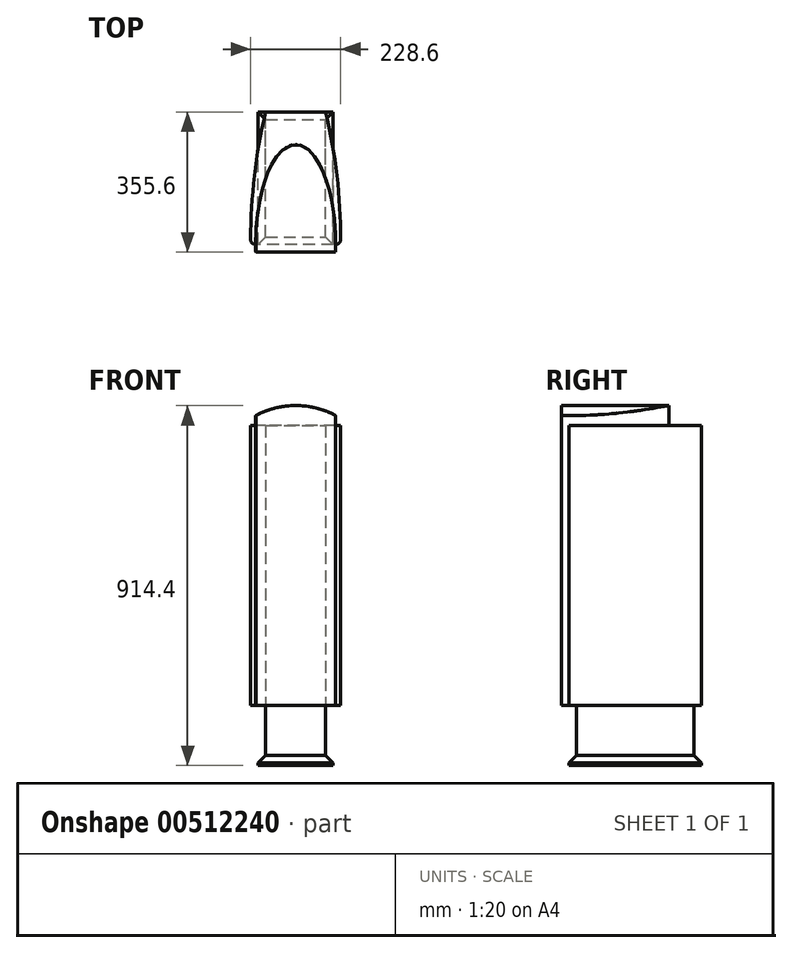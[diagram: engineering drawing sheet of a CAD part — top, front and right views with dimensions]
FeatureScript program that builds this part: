
annotation { "Feature Type Name" : "Feature", "Feature Type Description" : "" }
export const myFeature = defineFeature(function(context is Context, id is Id, definition is map)
    precondition{}
    {
        {
            var Q0;
            Q0=qCreatedBy(makeId("Top.planeOp"),FACE);
            var sketch = newSketch(context, id + "F0", { "sketchPlane" : qUnion([Q0])});
            skLineSegment(sketch, "E0.bottom", {"start": v(-114.3, -177.8) * mm, "end": v(114.3, -177.8) * mm});
            skLineSegment(sketch, "E0.top", {"start": v(-114.3, 177.8) * mm, "end": v(114.3, 177.8) * mm});
            skLineSegment(sketch, "E0.left", {"start": v(-114.3, -177.8) * mm, "end": v(-114.3, 177.8) * mm});
            skLineSegment(sketch, "E0.right", {"start": v(114.3, -177.8) * mm, "end": v(114.3, 177.8) * mm});
            skPoint(sketch, "E0.middle", {"position": v(0, 0) * mm});
            skLineSegment(sketch, "E1.bottom", {"start": v(-114.3, -177.8) * mm, "end": v(-101.6, -177.8) * mm});
            skLineSegment(sketch, "E1.top", {"start": v(-114.3, -146.05) * mm, "end": v(-101.6, -146.05) * mm});
            skLineSegment(sketch, "E1.left", {"start": v(-114.3, -177.8) * mm, "end": v(-114.3, -146.05) * mm});
            skLineSegment(sketch, "E1.right", {"start": v(-101.6, -177.8) * mm, "end": v(-101.6, -146.05) * mm});
            skArc(sketch, "E2", {"start": v(-114.3, -146.05) * mm, "mid": v(-104.74, 17) * mm, "end": v(-76.2, 177.8) * mm});
            skLineSegment(sketch, "E3.bottom", {"start": v(114.3, -177.8) * mm, "end": v(101.6, -177.8) * mm});
            skLineSegment(sketch, "E3.top", {"start": v(114.3, -146.05) * mm, "end": v(101.6, -146.05) * mm});
            skLineSegment(sketch, "E3.left", {"start": v(114.3, -177.8) * mm, "end": v(114.3, -146.05) * mm});
            skLineSegment(sketch, "E3.right", {"start": v(101.6, -177.8) * mm, "end": v(101.6, -146.05) * mm});
            skArc(sketch, "E4", {"start": v(114.3, -146.05) * mm, "mid": v(104.74, 17) * mm, "end": v(76.2, 177.8) * mm});
            skArc(sketch, "E5", {"start": v(-114.3, -146.05) * mm, "mid": v(-110.58, -155.03) * mm, "end": v(-101.6, -158.75) * mm});
            skArc(sketch, "E6", {"start": v(114.3, -146.05) * mm, "mid": v(110.58, -155.03) * mm, "end": v(101.6, -158.75) * mm});
            skLineSegment(sketch, "E7", {"start": v(-101.6, -158.75) * mm, "end": v(101.6, -158.75) * mm});
            skEllipse(sketch, "E8", {"center": v(0, -158.75) * mm, "majorRadius": 101.6 * mm, "minorRadius": 254 * mm, "majorAxis": v(-1, 0)});
            skLineSegment(sketch, "E9.bottom", {"start": v(-76.2, -139.7) * mm, "end": v(76.2, -139.7) * mm});
            skLineSegment(sketch, "E9.top", {"start": v(-76.2, 158.75) * mm, "end": v(76.2, 158.75) * mm});
            skLineSegment(sketch, "E9.left", {"start": v(-76.2, -139.7) * mm, "end": v(-76.2, 158.75) * mm});
            skLineSegment(sketch, "E9.right", {"start": v(76.2, -139.7) * mm, "end": v(76.2, 158.75) * mm});
            skSolve(sketch);
        }
        {
            var Q0;
            {var subQ7=sQuery(id+"F0.wireOp",EDGE,"E1.top");Q0=makeQuery(id+"F0.imprint","IMPRINT",FACE,{"disambiguationData":[TD([[makeQuery(id+"F0.imprint","IMPRINT",EDGE,{"derivedFrom":subQ7}),1.0]])]});}
            var Q1;
            {var subQ0=sQuery(id+"F0.wireOp",EDGE,"E1.top");Q1=makeQuery(id+"F0.imprint","IMPRINT",FACE,{"disambiguationData":[TD([[makeQuery(id+"F0.imprint","IMPRINT",EDGE,{"derivedFrom":subQ0}),-1.0]])]});}
            var Q2;
            {var subQ0=sQuery(id+"F0.wireOp",EDGE,"E3.top");Q2=makeQuery(id+"F0.imprint","IMPRINT",FACE,{"disambiguationData":[TD([[makeQuery(id+"F0.imprint","IMPRINT",EDGE,{"derivedFrom":subQ0}),1.0]])]});}
            var Q3;
            {var subQ5=sQuery(id+"F0.wireOp",EDGE,"E9.top");Q3=makeQuery(id+"F0.imprint","IMPRINT",FACE,{"disambiguationData":[TD([[makeQuery(id+"F0.imprint","IMPRINT",EDGE,{"derivedFrom":subQ5}),-1.0]])]});}
            extrude(context, id + "F1", {"entities" : qUnion([Q0, Q1, Q2, Q3]), "depth" : 711.2 * mm});
        }
        {
            var Q0;
            {var subQ0=sQuery(id+"F0.wireOp",EDGE,"E7");Q0=makeQuery(id+"F0.imprint","IMPRINT",FACE,{"disambiguationData":[TD([[makeQuery(id+"F0.imprint","IMPRINT",EDGE,{"derivedFrom":subQ0}),1.0]])]});}
            var Q1;
            {var subQ4=sQuery(id+"F0.wireOp",EDGE,"E7");Q1=makeQuery(id+"F0.imprint","IMPRINT",FACE,{"disambiguationData":[TD([[makeQuery(id+"F0.imprint","IMPRINT",EDGE,{"derivedFrom":subQ4}),-1.0]])]});}
            var Q2;
            {var subQ5=sQuery(id+"F0.wireOp",EDGE,"E9.bottom");Q2=makeQuery(id+"F0.imprint","IMPRINT",FACE,{"disambiguationData":[TD([[makeQuery(id+"F0.imprint","IMPRINT",EDGE,{"derivedFrom":subQ5}),1.0]])]});}
            extrude(context, id + "F2", {"entities" : qUnion([Q0, Q1, Q2]), "operationType" : NewBodyOperationType.ADD, "depth" : 762 * mm});
        }
        {
            var Q0;
            Q0=makeQuery(id+"F2.opExtrude","SWEPT_FACE",FACE,{"disambiguationData":[OSD([sQuery(id+"F0.wireOp",EDGE,"E0.bottom")])]});
            var sketch = newSketch(context, id + "F3", { "sketchPlane" : qUnion([Q0])});
            skArc(sketch, "E10", {"start": v(101.31, 736.6) * mm, "mid": v(0, 762) * mm, "end": v(-101.31, 736.6) * mm});
            skSolve(sketch);
        }
        {
            var Q0;
            {var subQ0=sQuery(id+"F3.wireOp",EDGE,"E10");var subQ2=sQuery(id+"F0.wireOp",EDGE,"E0.bottom");var subQ5=makeQuery(id+"F2.opExtrude","CAP_EDGE",EDGE,{"disambiguationData":[OSD([subQ2])],"isStart":false});var subQ6=makeQuery(id+"F3.imprint","INTERSECT",VERTEX,{"derivedFrom":[subQ5,subQ0]});Q0=makeQuery(id+"F3.imprint","IMPRINT",FACE,{"disambiguationData":[TD([[makeQuery(id+"F3.imprint","IMPRINT",EDGE,{"disambiguationData":[TD([[subQ6,-1.0]])],"derivedFrom":subQ0}),-1.0]])]});}
            var Q1;
            {var subQ0=sQuery(id+"F3.wireOp",EDGE,"E10");var subQ2=sQuery(id+"F0.wireOp",EDGE,"E0.bottom");var subQ5=makeQuery(id+"F2.opExtrude","CAP_EDGE",EDGE,{"disambiguationData":[OSD([subQ2])],"isStart":false});var subQ6=makeQuery(id+"F3.imprint","INTERSECT",VERTEX,{"derivedFrom":[subQ5,subQ0]});Q1=makeQuery(id+"F3.imprint","IMPRINT",FACE,{"disambiguationData":[TD([[makeQuery(id+"F3.imprint","IMPRINT",EDGE,{"disambiguationData":[TD([[subQ6,1.0]])],"derivedFrom":subQ0}),-1.0]])]});}
            extrude(context, id + "F4", {"entities" : qUnion([Q0, Q1]), "operationType" : NewBodyOperationType.REMOVE, "endBound" : BoundingType.UP_TO_NEXT, "oppositeDirection" : true, "depth" : 25.4 * mm});
        }
        {
            var Q0;
            {var subQ0=sQuery(id+"F0.wireOp",EDGE,"E0.bottom");var subQ1=sQuery(id+"F0.wireOp",EDGE,"E8");var subQ2=makeQuery(id+"F2.opExtrude","SWEPT_EDGE",EDGE,{"disambiguationData":[OSD([subQ0,subQ1]),TDD([makeQuery(id+"F0.imprint","INTERSECT",VERTEX,{"disambiguationData":[OD(0.0)],"derivedFrom":[subQ0,subQ1]})])]});Q0=makeQuery(id+"F4.boolean.opBoolean","COPY",FACE,{"derivedFrom":makeQuery(id+"F4.opExtrude","SWEPT_FACE",FACE,{"disambiguationData":[OSD([subQ0,subQ1]),TDD([makeQuery(id+"F3.imprint","IMPRINT",EDGE,{"disambiguationData":[TD([[makeQuery(id+"F3.imprint","INTERSECT",VERTEX,{"derivedFrom":[subQ2,makeQuery(id+"F2.opExtrude","CAP_EDGE",EDGE,{"disambiguationData":[OSD([subQ0])],"isStart":false})]}),-1.0]])],"derivedFrom":subQ2})])]})});}
            extrude(context, id + "F5", {"entities" : qUnion([Q0]), "operationType" : NewBodyOperationType.REMOVE, "endBound" : BoundingType.UP_TO_NEXT, "oppositeDirection" : true, "depth" : 25.4 * mm});
        }
        {
            var Q0;
            {var subQ0=sQuery(id+"F0.wireOp",EDGE,"E0.bottom");var subQ1=sQuery(id+"F0.wireOp",EDGE,"E8");var subQ2=makeQuery(id+"F2.opExtrude","SWEPT_EDGE",EDGE,{"disambiguationData":[OSD([subQ0,subQ1]),TDD([makeQuery(id+"F0.imprint","INTERSECT",VERTEX,{"disambiguationData":[OD(1.0)],"derivedFrom":[subQ0,subQ1]})])]});Q0=makeQuery(id+"F4.boolean.opBoolean","COPY",FACE,{"derivedFrom":makeQuery(id+"F4.opExtrude","SWEPT_FACE",FACE,{"disambiguationData":[OSD([subQ0,subQ1]),TDD([makeQuery(id+"F3.imprint","IMPRINT",EDGE,{"disambiguationData":[TD([[makeQuery(id+"F3.imprint","INTERSECT",VERTEX,{"derivedFrom":[subQ2,makeQuery(id+"F2.opExtrude","CAP_EDGE",EDGE,{"disambiguationData":[OSD([subQ0])],"isStart":false})]}),-1.0]])],"derivedFrom":subQ2})])]})});}
            extrude(context, id + "F6", {"entities" : qUnion([Q0]), "operationType" : NewBodyOperationType.REMOVE, "endBound" : BoundingType.UP_TO_NEXT, "oppositeDirection" : true, "depth" : 25.4 * mm});
        }
        {
            var Q0;
            {var subQ5=sQuery(id+"F0.wireOp",EDGE,"E9.bottom");Q0=makeQuery(id+"F0.imprint","IMPRINT",FACE,{"disambiguationData":[TD([[makeQuery(id+"F0.imprint","IMPRINT",EDGE,{"derivedFrom":subQ5}),1.0]])]});}
            var Q1;
            {var subQ5=sQuery(id+"F0.wireOp",EDGE,"E9.top");Q1=makeQuery(id+"F0.imprint","IMPRINT",FACE,{"disambiguationData":[TD([[makeQuery(id+"F0.imprint","IMPRINT",EDGE,{"derivedFrom":subQ5}),-1.0]])]});}
            extrude(context, id + "F7", {"entities" : qUnion([Q0, Q1]), "operationType" : NewBodyOperationType.ADD, "oppositeDirection" : true, "depth" : 152.4 * mm});
        }
        {
            var Q0;
            Q0=makeQuery(id+"F7.opExtrude","CAP_FACE",FACE,{"disambiguationData":[OSD([sQuery(id+"F0.wireOp",EDGE,"E9.bottom"),sQuery(id+"F0.wireOp",EDGE,"E9.top"),sQuery(id+"F0.wireOp",EDGE,"E9.left"),sQuery(id+"F0.wireOp",EDGE,"E9.right")])],"isStart":false});
            var sketch = newSketch(context, id + "F8", { "sketchPlane" : qUnion([Q0])});
            skLineSegment(sketch, "E11.bottom", {"start": v(-95.25, 158.75) * mm, "end": v(95.25, 158.75) * mm});
            skLineSegment(sketch, "E11.top", {"start": v(-95.25, -177.8) * mm, "end": v(95.25, -177.8) * mm});
            skLineSegment(sketch, "E11.left", {"start": v(-95.25, 158.75) * mm, "end": v(-95.25, -177.8) * mm});
            skLineSegment(sketch, "E11.right", {"start": v(95.25, 158.75) * mm, "end": v(95.25, -177.8) * mm});
            skSolve(sketch);
        }
        {
            var Q0;
            Q0=qSketchRegion(id+"F8",true);
            extrude(context, id + "F9", {"entities" : qUnion([Q0]), "operationType" : NewBodyOperationType.ADD, "oppositeDirection" : true, "depth" : 25.4 * mm});
        }
        {
            var Q0;
            Q0=makeQuery(id+"F9.opExtrude","CAP_EDGE",EDGE,{"disambiguationData":[OSD([sQuery(id+"F8.wireOp",EDGE,"E11.bottom")])],"isStart":false});
            var Q1;
            Q1=makeQuery(id+"F9.opExtrude","CAP_EDGE",EDGE,{"disambiguationData":[OSD([sQuery(id+"F8.wireOp",EDGE,"E11.right")])],"isStart":false});
            var Q2;
            Q2=makeQuery(id+"F9.opExtrude","CAP_EDGE",EDGE,{"disambiguationData":[OSD([sQuery(id+"F8.wireOp",EDGE,"E11.left")])],"isStart":false});
            var Q3;
            Q3=makeQuery(id+"F9.opExtrude","CAP_EDGE",EDGE,{"disambiguationData":[OSD([sQuery(id+"F8.wireOp",EDGE,"E11.top")])],"isStart":false});
            chamfer(context, id + "F10", {"entities" : qUnion([Q0, Q1, Q2, Q3]), "width" : 19.05 * mm, "tangentPropagation" : true});
        }
    });
